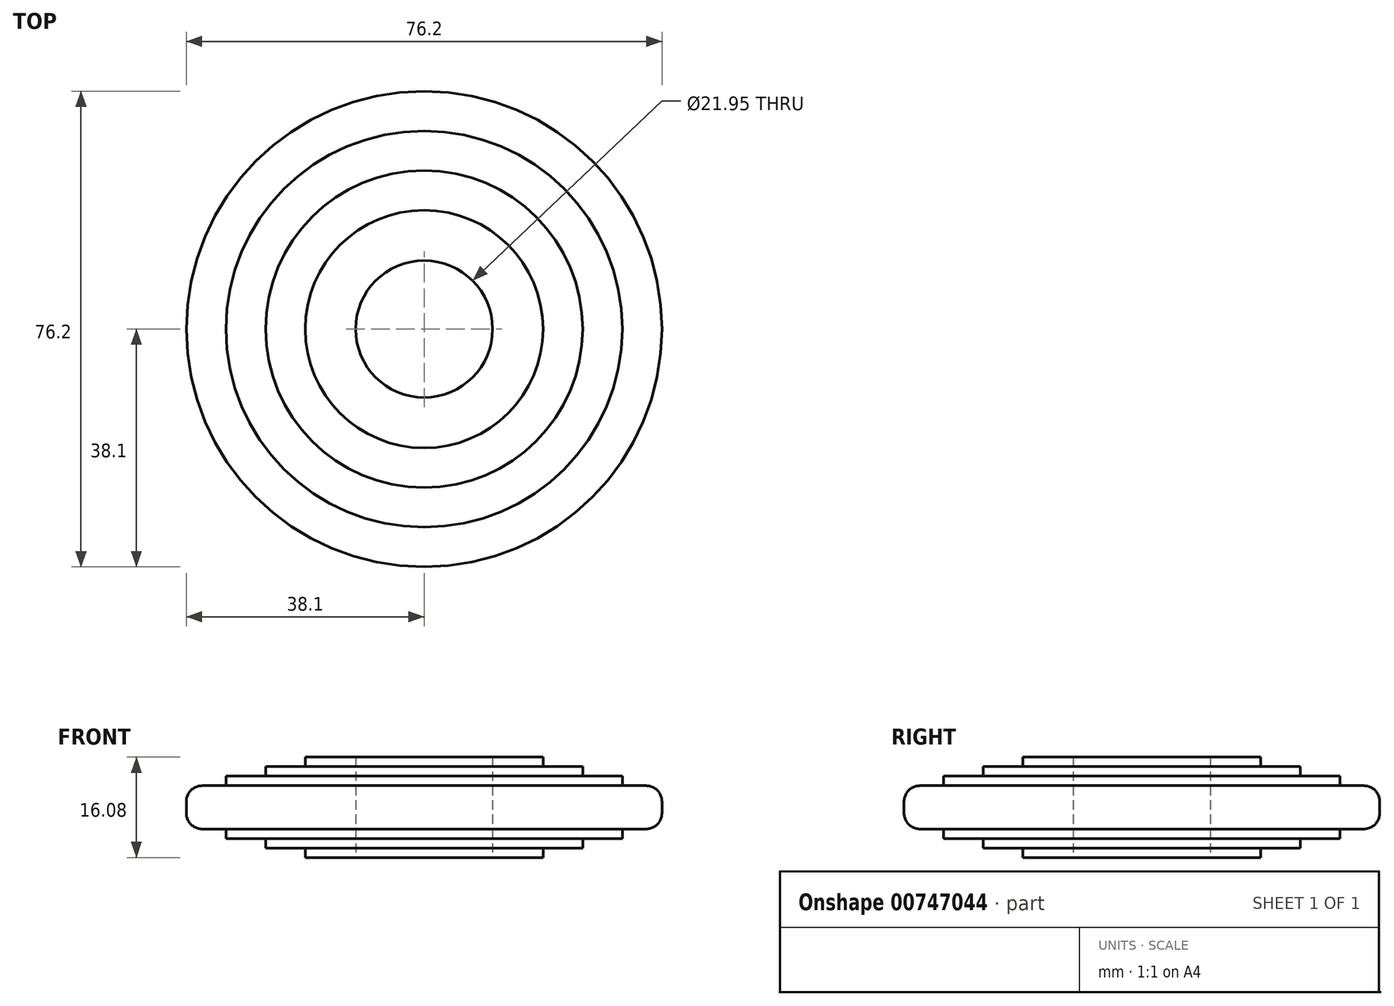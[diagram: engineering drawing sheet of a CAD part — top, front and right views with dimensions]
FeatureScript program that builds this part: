
annotation { "Feature Type Name" : "Feature", "Feature Type Description" : "" }
export const myFeature = defineFeature(function(context is Context, id is Id, definition is map)
    precondition{}
    {
        {
            var Q0;
            Q0=qCreatedBy(makeId("Top.planeOp"),FACE);
            var sketch = newSketch(context, id + "F0", { "sketchPlane" : qUnion([Q0])});
            skCircle(sketch, "E0", {"center": v(0, 0) * mm, "radius": 38.1 * mm});
            skSolve(sketch);
        }
        {
            var Q0;
            Q0 = qSketchRegion(id + "F0", true);
            extrude(context, id + "F1", {"entities" : qUnion([Q0]), "depth" : 6.93 * mm, "offsetDistance" : 25.4 * mm});
        }
        {
            var Q0;
            Q0=makeQuery(id+"F1.opExtrude","CAP_EDGE",EDGE,{"disambiguationData":[OSD([sQuery(id+"F0.wireOp",EDGE,"E0")])],"isStart":false});
            var Q1;
            Q1=makeQuery(id+"F1.opExtrude","CAP_FACE",FACE,{"disambiguationData":[OSD([sQuery(id+"F0.wireOp",EDGE,"E0")])],"isStart":true});
            fillet(context, id + "F2", {"entities" : qUnion([Q0, Q1]), "radius" : 2.54 * mm, "tangentPropagation" : true, "allowEdgeOverflow" : false});
        }
        {
            var Q0;
            Q0=makeQuery(id+"F1.opExtrude","CAP_FACE",FACE,{"disambiguationData":[OSD([sQuery(id+"F0.wireOp",EDGE,"E0")])],"isStart":false});
            var sketch = newSketch(context, id + "F3", { "sketchPlane" : qUnion([Q0])});
            skCircle(sketch, "E1", {"center": v(0, 0) * mm, "radius": 31.75 * mm});
            skSolve(sketch);
        }
        {
            var Q0;
            Q0 = qSketchRegion(id + "F3", true);
            extrude(context, id + "F4", {"entities" : qUnion([Q0]), "operationType" : NewBodyOperationType.ADD, "depth" : 1.52 * mm, "offsetDistance" : 25.4 * mm});
        }
        {
            var Q0;
            Q0=makeQuery(id+"F4.opExtrude","CAP_FACE",FACE,{"disambiguationData":[OSD([sQuery(id+"F3.wireOp",EDGE,"E1")])],"isStart":false});
            var sketch = newSketch(context, id + "F5", { "sketchPlane" : qUnion([Q0])});
            skCircle(sketch, "E2", {"center": v(0, 0) * mm, "radius": 25.4 * mm});
            skSolve(sketch);
        }
        {
            var Q0;
            Q0=makeQuery(id+"F4.opExtrude","CAP_FACE",FACE,{"disambiguationData":[OSD([sQuery(id+"F3.wireOp",EDGE,"E1")])],"isStart":false});
            var sketch = newSketch(context, id + "F6", { "sketchPlane" : qUnion([Q0])});
            skCircle(sketch, "E3", {"center": v(0, 0) * mm, "radius": 19.05 * mm});
            skSolve(sketch);
        }
        {
            var Q0;
            Q0 = qSketchRegion(id + "F6", true);
            extrude(context, id + "F7", {"entities" : qUnion([Q0]), "operationType" : NewBodyOperationType.ADD, "depth" : 1.52 * mm, "offsetDistance" : 25.4 * mm});
        }
        {
            var Q0;
            Q0 = qSketchRegion(id + "F5", true);
            extrude(context, id + "F8", {"entities" : qUnion([Q0]), "operationType" : NewBodyOperationType.ADD, "depth" : 1.52 * mm, "offsetDistance" : 25.4 * mm});
        }
        {
            var Q0;
            Q0=makeQuery(id+"F8.boolean.opBoolean","MERGE",FACE,{"derivedFrom":[makeQuery(id+"F7.opExtrude","CAP_FACE",FACE,{"disambiguationData":[OSD([sQuery(id+"F6.wireOp",EDGE,"E3")])],"isStart":false}),makeQuery(id+"F8.opExtrude","CAP_FACE",FACE,{"disambiguationData":[OSD([sQuery(id+"F5.wireOp",EDGE,"E2")])],"isStart":false})]});
            var sketch = newSketch(context, id + "F9", { "sketchPlane" : qUnion([Q0])});
            skCircle(sketch, "E4", {"center": v(0, 0) * mm, "radius": 19.05 * mm});
            skSolve(sketch);
        }
        {
            var Q0;
            Q0 = qSketchRegion(id + "F9", true);
            extrude(context, id + "F10", {"entities" : qUnion([Q0]), "operationType" : NewBodyOperationType.ADD, "depth" : 1.52 * mm, "offsetDistance" : 25.4 * mm});
        }
        {
            var Q0;
            Q0=makeQuery(id+"F1.opExtrude","CAP_FACE",FACE,{"disambiguationData":[OSD([sQuery(id+"F0.wireOp",EDGE,"E0")])],"isStart":true});
            var sketch = newSketch(context, id + "F11", { "sketchPlane" : qUnion([Q0])});
            skCircle(sketch, "E5", {"center": v(0, 0) * mm, "radius": 31.75 * mm});
            skSolve(sketch);
        }
        {
            var Q0;
            Q0 = qSketchRegion(id + "F11", true);
            extrude(context, id + "F12", {"entities" : qUnion([Q0]), "operationType" : NewBodyOperationType.ADD, "depth" : 1.52 * mm, "offsetDistance" : 25.4 * mm});
        }
        {
            var Q0;
            Q0=makeQuery(id+"F12.opExtrude","CAP_FACE",FACE,{"disambiguationData":[OSD([sQuery(id+"F11.wireOp",EDGE,"E5")])],"isStart":false});
            var sketch = newSketch(context, id + "F13", { "sketchPlane" : qUnion([Q0])});
            skCircle(sketch, "E6", {"center": v(0, 0) * mm, "radius": 25.4 * mm});
            skSolve(sketch);
        }
        {
            var Q0;
            Q0 = qSketchRegion(id + "F13", true);
            extrude(context, id + "F14", {"entities" : qUnion([Q0]), "operationType" : NewBodyOperationType.ADD, "depth" : 1.52 * mm, "offsetDistance" : 25.4 * mm});
        }
        {
            var Q0;
            Q0=makeQuery(id+"F14.opExtrude","CAP_FACE",FACE,{"disambiguationData":[OSD([sQuery(id+"F13.wireOp",EDGE,"E6")])],"isStart":false});
            var sketch = newSketch(context, id + "F15", { "sketchPlane" : qUnion([Q0])});
            skCircle(sketch, "E7", {"center": v(0, 0) * mm, "radius": 19.05 * mm});
            skSolve(sketch);
        }
        {
            var Q0;
            Q0 = qSketchRegion(id + "F15", true);
            extrude(context, id + "F16", {"entities" : qUnion([Q0]), "operationType" : NewBodyOperationType.ADD, "depth" : 1.52 * mm, "offsetDistance" : 25.4 * mm});
        }
        {
            var Q0;
            Q0=makeQuery(id+"F16.opExtrude","CAP_FACE",FACE,{"disambiguationData":[OSD([sQuery(id+"F15.wireOp",EDGE,"E7")])],"isStart":false});
            var sketch = newSketch(context, id + "F17", { "sketchPlane" : qUnion([Q0])});
            skCircle(sketch, "E8", {"center": v(0, 0) * mm, "radius": 10.97 * mm});
            skSolve(sketch);
        }
        {
            var Q0;
            Q0 = qSketchRegion(id + "F17", true);
            extrude(context, id + "F18", {"entities" : qUnion([Q0]), "operationType" : NewBodyOperationType.REMOVE, "oppositeDirection" : true, "depth" : 25.4 * mm, "offsetDistance" : 25.4 * mm});
        }
    });
